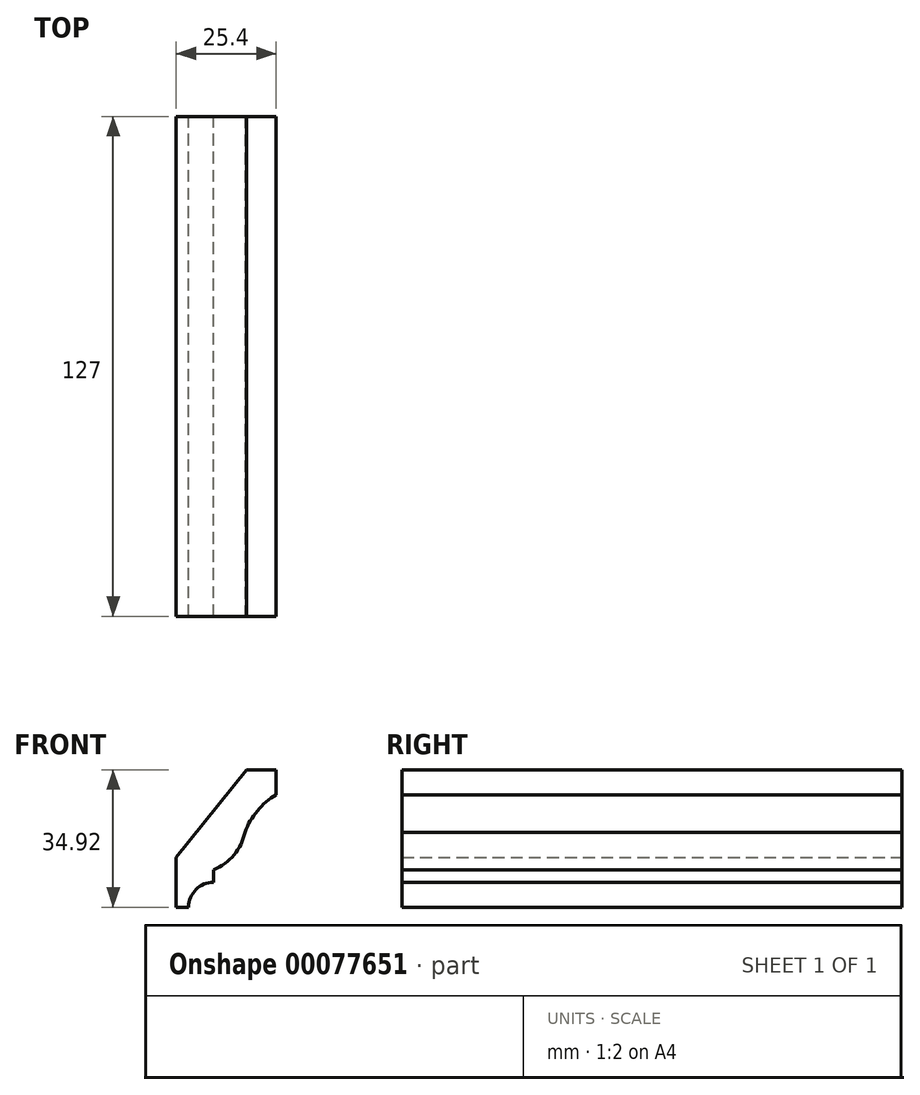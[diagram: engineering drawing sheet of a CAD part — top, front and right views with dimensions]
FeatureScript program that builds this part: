
annotation { "Feature Type Name" : "Feature", "Feature Type Description" : "" }
export const myFeature = defineFeature(function(context is Context, id is Id, definition is map)
    precondition{}
    {
        {
            var Q0;
            Q0=qCreatedBy(makeId("Front.planeOp"),FACE);
            var sketch = newSketch(context, id + "F0", { "sketchPlane" : qUnion([Q0])});
            skLineSegment(sketch, "E0", {"start": v(5.2, 17.46) * mm, "end": v(12.7, 17.46) * mm});
            skLineSegment(sketch, "E1", {"start": v(12.7, 17.46) * mm, "end": v(12.7, 11.11) * mm});
            skLineSegment(sketch, "E2", {"start": v(-12.7, -4.76) * mm, "end": v(-12.7, -17.46) * mm});
            skLineSegment(sketch, "E3", {"start": v(-12.7, -17.46) * mm, "end": v(-9.53, -17.46) * mm});
            skLineSegment(sketch, "E4", {"start": v(-12.7, -4.76) * mm, "end": v(5.2, 17.46) * mm});
            skLineSegment(sketch, "E5", {"start": v(-3.18, -11.11) * mm, "end": v(-3.18, -7.94) * mm});
            skArc(sketch, "E6", {"start": v(-3.18, -11.11) * mm, "mid": v(-7.67, -12.97) * mm, "end": v(-9.53, -17.46) * mm});
            skArc(sketch, "E7", {"start": v(-3.18, -7.94) * mm, "mid": v(2, -4.18) * mm, "end": v(4.76, 1.59) * mm});
            skArc(sketch, "E8", {"start": v(12.7, 11.11) * mm, "mid": v(7.93, 7.02) * mm, "end": v(4.76, 1.59) * mm});
            skSolve(sketch);
        }
        {
            var Q0;
            Q0=makeQuery(id+"F0.imprint","IMPRINT",FACE,{"disambiguationData":[TD([[makeQuery(id+"F0.imprint","IMPRINT",EDGE,{"derivedFrom":sQuery(id+"F0.wireOp",EDGE,"E0")}),-1.0]])]});
            extrude(context, id + "F1", {"entities" : qUnion([Q0]), "depth" : 127 * mm});
        }
    });
